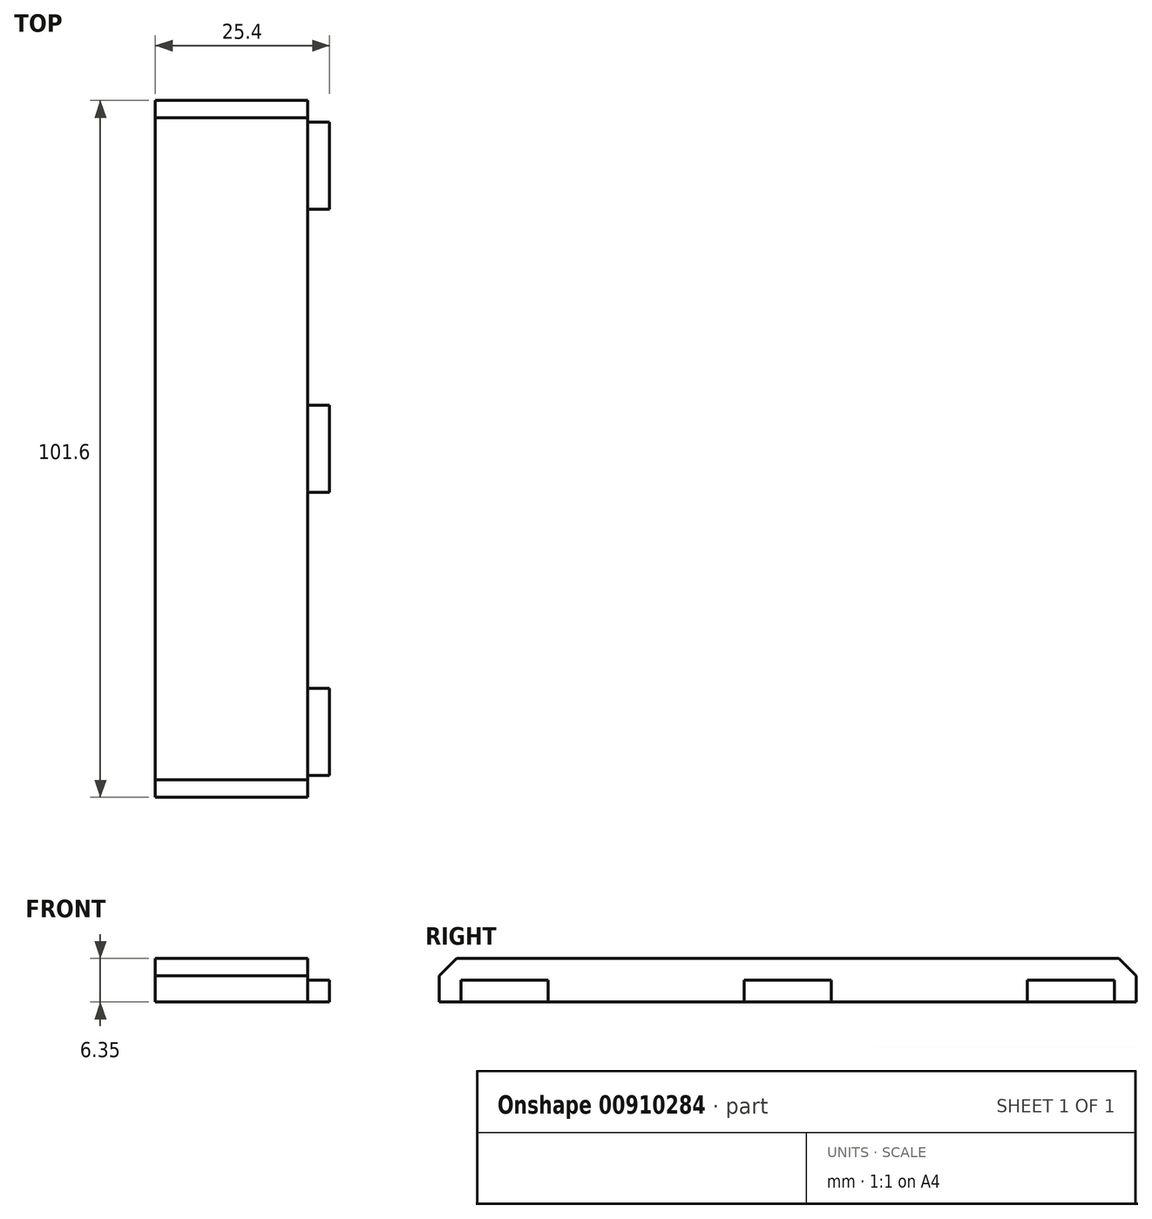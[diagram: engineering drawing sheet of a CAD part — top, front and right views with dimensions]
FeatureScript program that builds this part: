
annotation { "Feature Type Name" : "Feature", "Feature Type Description" : "" }
export const myFeature = defineFeature(function(context is Context, id is Id, definition is map)
    precondition{}
    {
        {
            var Q0;
            Q0=qCreatedBy(makeId("Top.planeOp"),FACE);
            var sketch = newSketch(context, id + "F0", { "sketchPlane" : qUnion([Q0])});
            skLineSegment(sketch, "E0.bottom", {"start": v(-11.11, -50.8) * mm, "end": v(11.11, -50.8) * mm});
            skLineSegment(sketch, "E0.top", {"start": v(-11.11, 50.8) * mm, "end": v(11.11, 50.8) * mm});
            skLineSegment(sketch, "E0.left", {"start": v(-11.11, -50.8) * mm, "end": v(-11.11, 50.8) * mm});
            skLineSegment(sketch, "E0.right", {"start": v(11.11, -50.8) * mm, "end": v(11.11, 50.8) * mm});
            skLineSegment(sketch, "E1", {"start": v(-11.11, 50.8) * mm, "end": v(11.11, -50.8) * mm, "construction": true});
            skLineSegment(sketch, "E2", {"start": v(-11.11, -50.8) * mm, "end": v(11.11, 50.8) * mm, "construction": true});
            skPoint(sketch, "E3", {"position": v(0, 0) * mm});
            skSolve(sketch);
        }
        {
            var Q0;
            Q0 = qSketchRegion(id + "F0", true);
            extrude(context, id + "F1", {"entities" : qUnion([Q0]), "depth" : 6.35 * mm, "offsetDistance" : 25.4 * mm});
        }
        {
            var Q0;
            Q0=makeQuery(id+"F1.opExtrude","SWEPT_FACE",FACE,{"disambiguationData":[OSD([sQuery(id+"F0.wireOp",EDGE,"E0.right")])]});
            var sketch = newSketch(context, id + "F2", { "sketchPlane" : qUnion([Q0])});
            skLineSegment(sketch, "E4.bottom", {"start": v(-47.63, 0) * mm, "end": v(-34.93, 0) * mm});
            skLineSegment(sketch, "E4.top", {"start": v(-47.63, 3.17) * mm, "end": v(-34.93, 3.18) * mm});
            skLineSegment(sketch, "E4.left", {"start": v(-47.63, 0) * mm, "end": v(-47.63, 3.17) * mm});
            skLineSegment(sketch, "E4.right", {"start": v(-34.93, 0) * mm, "end": v(-34.93, 3.18) * mm});
            skLineSegment(sketch, "E5.bottom", {"start": v(-6.35, 0) * mm, "end": v(6.35, 0) * mm});
            skLineSegment(sketch, "E5.top", {"start": v(-6.35, 3.18) * mm, "end": v(6.35, 3.18) * mm});
            skLineSegment(sketch, "E5.left", {"start": v(-6.35, 0) * mm, "end": v(-6.35, 3.18) * mm});
            skLineSegment(sketch, "E5.right", {"start": v(6.35, 0) * mm, "end": v(6.35, 3.18) * mm});
            skLineSegment(sketch, "E6.bottom", {"start": v(47.63, 0) * mm, "end": v(34.93, 0) * mm});
            skLineSegment(sketch, "E6.top", {"start": v(47.63, 3.18) * mm, "end": v(34.93, 3.17) * mm});
            skLineSegment(sketch, "E6.left", {"start": v(47.63, 0) * mm, "end": v(47.63, 3.18) * mm});
            skLineSegment(sketch, "E6.right", {"start": v(34.93, 0) * mm, "end": v(34.93, 3.17) * mm});
            skSolve(sketch);
        }
        {
            var Q0;
            Q0 = qSketchRegion(id + "F2", true);
            extrude(context, id + "F3", {"entities" : qUnion([Q0]), "operationType" : NewBodyOperationType.ADD, "depth" : 3.17 * mm, "offsetDistance" : 25.4 * mm});
        }
        {
            var Q0;
            Q0=makeQuery(id+"F1.opExtrude","CAP_EDGE",EDGE,{"disambiguationData":[OSD([sQuery(id+"F0.wireOp",EDGE,"E0.top")])],"isStart":false});
            var Q1;
            Q1=makeQuery(id+"F1.opExtrude","CAP_EDGE",EDGE,{"disambiguationData":[OSD([sQuery(id+"F0.wireOp",EDGE,"E0.bottom")])],"isStart":false});
            chamfer(context, id + "F4", {"entities" : qUnion([Q0, Q1]), "width" : 2.54 * mm, "tangentPropagation" : true});
        }
    });
